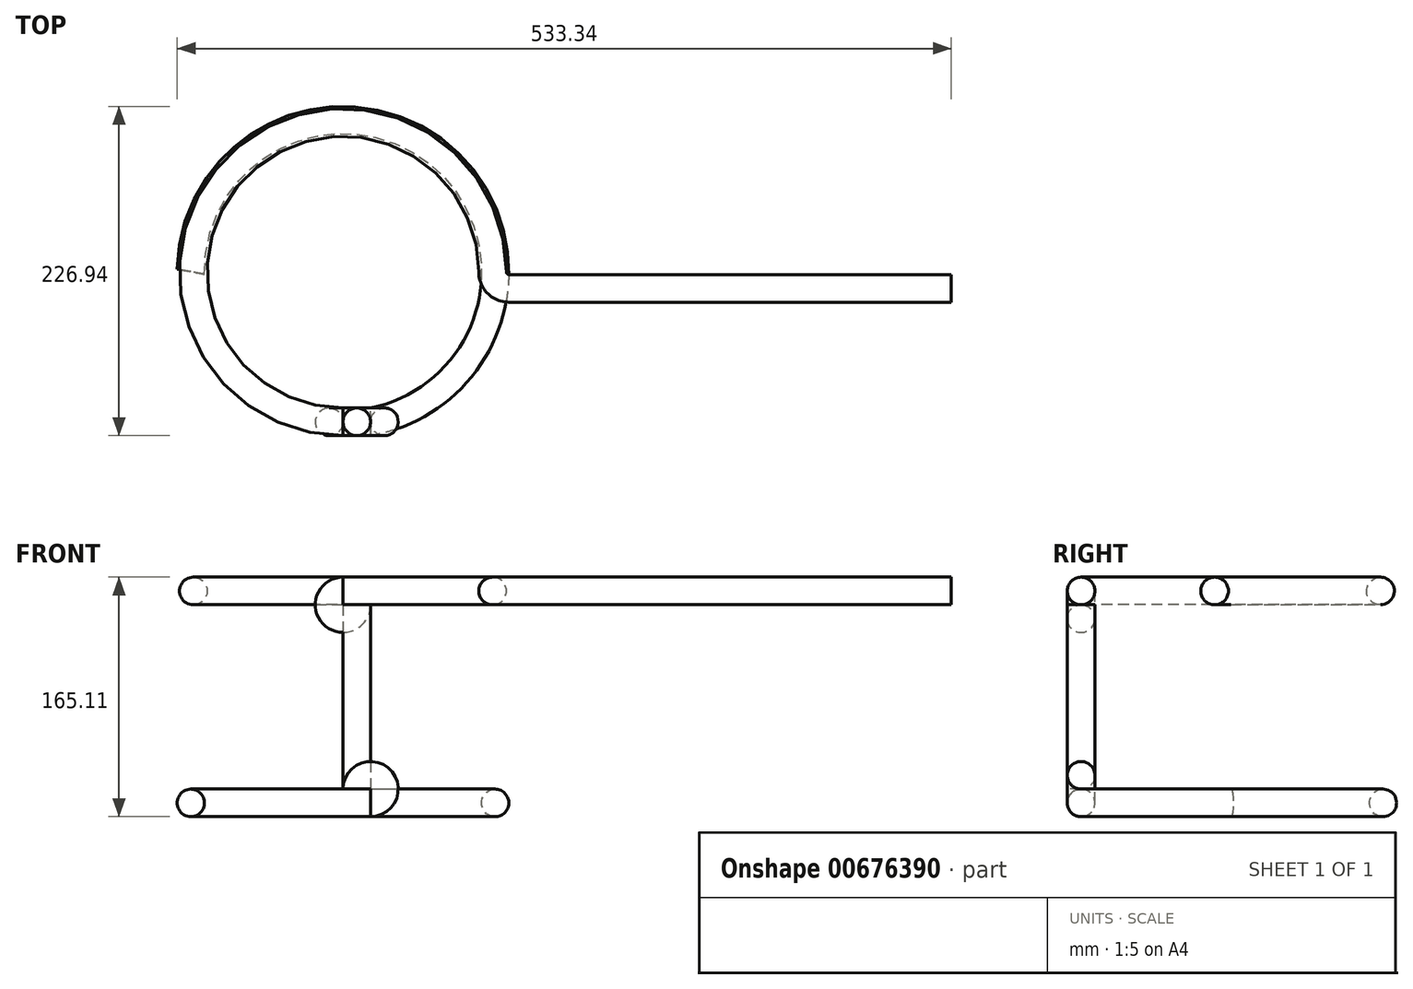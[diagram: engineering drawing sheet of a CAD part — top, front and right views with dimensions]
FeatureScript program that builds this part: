
annotation { "Feature Type Name" : "Feature", "Feature Type Description" : "" }
export const myFeature = defineFeature(function(context is Context, id is Id, definition is map)
    precondition{}
    {
        {
            var Q0;
            Q0=qCreatedBy(makeId("Top.planeOp"),FACE);
            var sketch = newSketch(context, id + "F0", { "sketchPlane" : qUnion([Q0])});
            skArc(sketch, "E0", {"start": v(103.14, 0) * mm, "mid": v(-72.93, 72.93) * mm, "end": v(0, -103.14) * mm});
            skSolve(sketch);
        }
        {
            var Q0;
            Q0=qCreatedBy(makeId("Front.planeOp"),FACE);
            var sketch = newSketch(context, id + "F1", { "sketchPlane" : qUnion([Q0])});
            skCircle(sketch, "E1", {"center": v(103.14, 0) * mm, "radius": 9.53 * mm});
            skSolve(sketch);
        }
        {
            var Q0;
            Q0=makeQuery(id+"F1.imprint","IMPRINT",FACE,{"disambiguationData":[TD([[makeQuery(id+"F1.imprint","IMPRINT",EDGE,{"derivedFrom":sQuery(id+"F1.wireOp",EDGE,"E1")}),1.0]])]});
            var Q1;
            Q1=sQuery(id+"F0.wireOp",EDGE,"E0");
            sweep(context, id + "F2", {"profiles" : qUnion([Q0]), "path" : qUnion([Q1])});
        }
        {
            var Q0;
            Q0=qCreatedBy(makeId("Front.planeOp"),FACE);
            cPlane(context, id + "F3", {"entities" : qUnion([Q0]), "cplaneType" : CPlaneType.OFFSET, "offset" : 103.14 * mm, "width" : 152.4 * mm, "height" : 152.4 * mm});
        }
        {
            var Q0;
            Q0=qCreatedBy(id+"F3.planeOp",FACE);
            var sketch = newSketch(context, id + "F4", { "sketchPlane" : qUnion([Q0])});
            skArc(sketch, "E2", {"start": v(9.53, -9.53) * mm, "mid": v(6.74, -2.79) * mm, "end": v(0, 0) * mm});
            skLineSegment(sketch, "E3", {"start": v(9.53, -9.53) * mm, "end": v(9.53, -136.53) * mm});
            skSolve(sketch);
        }
        {
            var Q0;
            Q0=makeQuery(id+"F2.opSweep","CAP_FACE",FACE,{"disambiguationData":[OSD([sQuery(id+"F0.wireOp",VERTEX,"E0.end"),sQuery(id+"F1.wireOp",EDGE,"E1")])],"isStart":false});
            var Q1;
            Q1=sQuery(id+"F4.wireOp",EDGE,"E2");
            var Q2;
            Q2=sQuery(id+"F4.wireOp",EDGE,"E3");
            sweep(context, id + "F5", {"operationType" : NewBodyOperationType.ADD, "profiles" : qUnion([Q0]), "path" : qUnion([Q1, Q2])});
        }
        {
            var Q0;
            Q0=qCreatedBy(id+"F3.planeOp",FACE);
            var sketch = newSketch(context, id + "F6", { "sketchPlane" : qUnion([Q0])});
            skLineSegment(sketch, "E4", {"start": v(9.53, -136.53) * mm, "end": v(9.53, -188.55) * mm, "construction": true});
            skArc(sketch, "E5.MirrorCS", {"start": v(19.05, -146.05) * mm, "mid": v(12.31, -143.26) * mm, "end": v(9.53, -136.53) * mm});
            skSolve(sketch);
        }
        {
            var Q0;
            Q0=qCreatedBy(makeId("Top.planeOp"),FACE);
            cPlane(context, id + "F7", {"entities" : qUnion([Q0]), "cplaneType" : CPlaneType.OFFSET, "offset" : 146.05 * mm, "oppositeDirection" : true, "width" : 152.4 * mm, "height" : 152.4 * mm});
        }
        {
            var Q0;
            Q0=qCreatedBy(id+"F7.planeOp",FACE);
            var sketch = newSketch(context, id + "F8", { "sketchPlane" : qUnion([Q0])});
            skArc(sketch, "E6", {"start": v(18.96, -101.38) * mm, "mid": v(65.89, 79.35) * mm, "end": v(-103.14, 0) * mm});
            skLineSegment(sketch, "E7", {"start": v(0, 0) * mm, "end": v(25.16, -100.02) * mm});
            skSolve(sketch);
        }
        {
            var Q0;
            Q0=makeQuery(id+"F5.opSweep","CAP_FACE",FACE,{"disambiguationData":[OSD([sQuery(id+"F0.wireOp",VERTEX,"E0.end"),sQuery(id+"F1.wireOp",EDGE,"E1"),sQuery(id+"F4.wireOp",VERTEX,"E3.end")])],"isStart":false});
            var Q1;
            Q1=sQuery(id+"F6.wireOp",EDGE,"E5.MirrorCS");
            sweep(context, id + "F9", {"operationType" : NewBodyOperationType.ADD, "profiles" : qUnion([Q0]), "path" : qUnion([Q1])});
        }
        {
            var Q0;
            Q0=makeQuery(id+"F9.opSweep","CAP_FACE",FACE,{"disambiguationData":[OSD([sQuery(id+"F0.wireOp",VERTEX,"E0.end"),sQuery(id+"F1.wireOp",EDGE,"E1"),sQuery(id+"F4.wireOp",VERTEX,"E3.end"),sQuery(id+"F6.wireOp",VERTEX,"E5.MirrorCS.start")])],"isStart":false});
            var Q1;
            Q1=sQuery(id+"F8.wireOp",EDGE,"E6");
            sweep(context, id + "F10", {"operationType" : NewBodyOperationType.ADD, "profiles" : qUnion([Q0]), "path" : qUnion([Q1])});
        }
        {
            var Q0;
            Q0=qCreatedBy(makeId("Top.planeOp"),FACE);
            var sketch = newSketch(context, id + "F11", { "sketchPlane" : qUnion([Q0])});
            skArc(sketch, "E8", {"start": v(104.78, 0) * mm, "mid": v(107.56, -6.74) * mm, "end": v(114.3, -9.53) * mm});
            skPoint(sketch, "E9.start.orphan", {"position": v(95.25, 0) * mm});
            skLineSegment(sketch, "E10", {"start": v(114.3, -9.53) * mm, "end": v(419.1, -9.53) * mm});
            skSolve(sketch);
        }
        {
            var Q0;
            Q0=makeQuery(id+"F2.opSweep","CAP_FACE",FACE,{"disambiguationData":[OSD([sQuery(id+"F0.wireOp",VERTEX,"E0.start"),sQuery(id+"F1.wireOp",EDGE,"E1")])],"isStart":true});
            var Q1;
            Q1=sQuery(id+"F11.wireOp",EDGE,"E8");
            var Q2;
            Q2=sQuery(id+"F11.wireOp",EDGE,"E10");
            sweep(context, id + "F12", {"operationType" : NewBodyOperationType.ADD, "profiles" : qUnion([Q0]), "path" : qUnion([Q1, Q2])});
        }
        {
            var Q0;
            Q0=qCreatedBy(makeId("Top.planeOp"),FACE);
            cPlane(context, id + "F13", {"entities" : qUnion([Q0]), "cplaneType" : CPlaneType.OFFSET, "offset" : 9.52 * mm, "oppositeDirection" : true, "width" : 152.4 * mm, "height" : 152.4 * mm});
        }
    });
